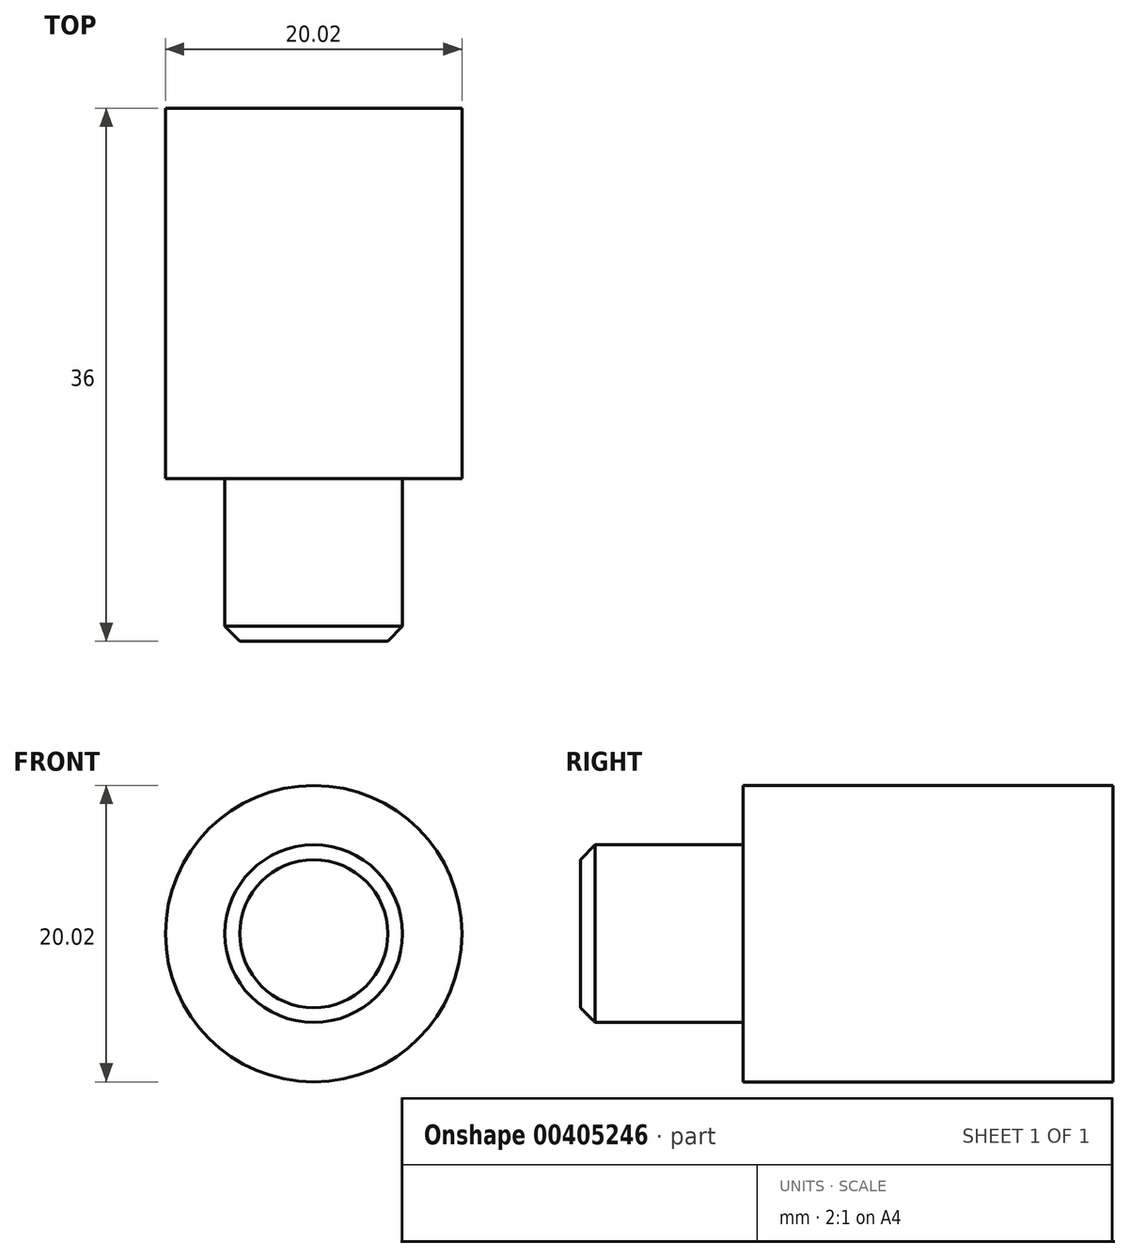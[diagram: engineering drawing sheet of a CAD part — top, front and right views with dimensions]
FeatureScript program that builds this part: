
annotation { "Feature Type Name" : "Feature", "Feature Type Description" : "" }
export const myFeature = defineFeature(function(context is Context, id is Id, definition is map)
    precondition{}
    {
        {
            var Q0;
            Q0=qCreatedBy(makeId("Front.planeOp"),FACE);
            var sketch = newSketch(context, id + "F0", { "sketchPlane" : qUnion([Q0])});
            skCircle(sketch, "E0", {"center": v(0, 0) * mm, "radius": 10 * mm});
            skSolve(sketch);
        }
        {
            var Q0;
            Q0=makeQuery(id+"F0.imprint","IMPRINT",FACE,{"disambiguationData":[TD([[makeQuery(id+"F0.imprint","IMPRINT",EDGE,{"derivedFrom":sQuery(id+"F0.wireOp",EDGE,"E0")}),1.0]])]});
            extrude(context, id + "F1", {"entities" : qUnion([Q0]), "depth" : 25 * mm});
        }
        {
            var Q0;
            Q0=makeQuery(id+"F1.opExtrude","CAP_FACE",FACE,{"disambiguationData":[OSD([sQuery(id+"F0.wireOp",EDGE,"E0")])],"isStart":false});
            var sketch = newSketch(context, id + "F2", { "sketchPlane" : qUnion([Q0])});
            skCircle(sketch, "E1", {"center": v(0, 0) * mm, "radius": 6 * mm});
            skSolve(sketch);
        }
        {
            var Q0;
            Q0=makeQuery(id+"F2.imprint","IMPRINT",FACE,{"disambiguationData":[TD([[makeQuery(id+"F2.imprint","IMPRINT",EDGE,{"derivedFrom":sQuery(id+"F2.wireOp",EDGE,"E1")}),1.0]])]});
            extrude(context, id + "F3", {"entities" : qUnion([Q0]), "operationType" : NewBodyOperationType.ADD, "depth" : 11 * mm});
        }
        {
            var Q0;
            Q0=makeQuery(id+"F3.opExtrude","CAP_FACE",FACE,{"disambiguationData":[OSD([sQuery(id+"F2.wireOp",EDGE,"E1")])],"isStart":false});
            chamfer(context, id + "F4", {"entities" : qUnion([Q0]), "chamferType" : ChamferType.OFFSET_ANGLE, "width" : 1 * mm, "oppositeDirection" : false, "angle" : 45 * degree, "tangentPropagation" : true});
        }
    });
